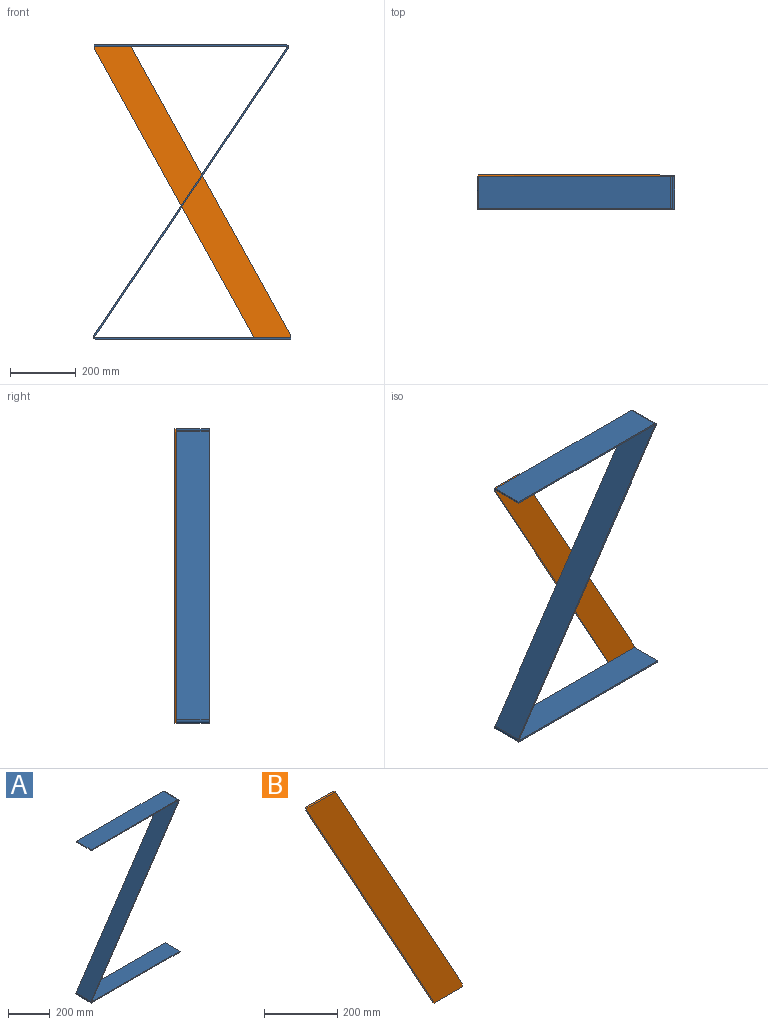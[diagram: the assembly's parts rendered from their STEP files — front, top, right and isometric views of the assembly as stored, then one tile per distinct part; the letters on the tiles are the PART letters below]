
ASSEMBLY  parts=2 mates=1
PART A: 22 faces, bbox 603x100x898 mm
  f0: plane 586.3x5mm, normal (0,1,0), area 2931.5mm2, adj f2,f3,f4,f19
  f1: plane 586.3x5mm, normal (0,-1,0), area 2931.5mm2, adj f2,f3,f4,f18
  f2: plane 100x5mm, normal (-1,0,0), area 500mm2, adj f0,f1,f3,f4
  f3: plane 586.3x100mm, normal (0,0,-1), area 58630mm2, adj f0,f1,f2,f21
  f4: plane 586.3x100mm, normal (0,0,1), area 58630mm2, adj f0,f1,f2,f20
  f5: plane 880.83x594.1mm, normal (0,1,0), area 5289.2mm2, adj f7,f8,f15,f19
  f6: plane 880.83x594.1mm, normal (0,-1,0), area 5289.2mm2, adj f7,f8,f14,f18
  f7: plane 878.05x589.95mm, normal (-0.83,0,0.56), area 105783.2mm2, adj f5,f6,f16,f21
  f8: plane 878.05x589.95mm, normal (0.83,0,-0.56), area 105783.2mm2, adj f5,f6,f17,f20
  f9: plane 595.68x5mm, normal (0,1,0), area 2978.4mm2, adj f10,f12,f13,f15
  f10: plane 100x5mm, normal (1,0,0), area 500mm2, adj f9,f11,f12,f13
  f11: plane 595.68x5mm, normal (0,-1,0), area 2978.4mm2, adj f10,f12,f13,f14
  f12: plane 595.68x100mm, normal (0,0,-1), area 59568.4mm2, adj f9,f10,f11,f16
  f13: plane 595.68x100mm, normal (0,0,1), area 59568.4mm2, adj f9,f10,f11,f17
  f14: plane 11.37x7.3mm, normal (0,-1,0), area 51.9mm2, adj f6,f11,f16,f17
  f15: plane 11.37x7.3mm, normal (0,1,0), area 51.9mm2, adj f5,f9,f16,f17
  f16: cylinder r=7.3mm len=100mm, axis (0,-1,0), area 1578.6mm2, adj f7,f12,f14,f15
  f17: cylinder r=2.3mm len=100mm, axis (0,-1,0), area 497.4mm2, adj f8,f13,f14,f15
  f18: plane 11.37x7.3mm, normal (0,-1,0), area 51.9mm2, adj f1,f6,f20,f21
  f19: plane 11.37x7.3mm, normal (0,1,0), area 51.9mm2, adj f0,f5,f20,f21
  f20: cylinder r=7.3mm len=100mm, axis (0,-1,0), area 1578.6mm2, adj f4,f8,f18,f19
  f21: cylinder r=2.3mm len=100mm, axis (0,-1,0), area 497.4mm2, adj f3,f7,f18,f19
PART B: 8 faces, bbox 600x5x898 mm
  f0: plane 888x491.25mm, normal (-0.88,0,-0.48), area 5074.1mm2, adj f1,f5,f6,f7
  f1: plane 10x5mm, normal (-1,0,0), area 50mm2, adj f0,f2,f6,f7
  f2: plane 108.75x5mm, normal (0,0,1), area 543.8mm2, adj f1,f3,f6,f7
  f3: plane 888x491.25mm, normal (0.88,0,0.48), area 5074.1mm2, adj f2,f4,f6,f7
  f4: plane 10x5mm, normal (1,0,0), area 50mm2, adj f3,f5,f6,f7
  f5: plane 108.75x5mm, normal (0,0,-1), area 543.8mm2, adj f0,f4,f6,f7
  f6: plane 898x600mm, normal (0,1,0), area 102570mm2, adj f0,f1,f2,f3,f4,f5
  f7: plane 898x600mm, normal (0,-1,0), area 102570mm2, adj f0,f1,f2,f3,f4,f5
PLACE A t=(-718.17,-633.33,203.4)mm
PLACE B t=(-718.17,-628.33,203.4)mm
MATE parallel B.f7 <-> A.f0  axis (0,-1,0) through (-718.17,-633.33,203.4)mm
